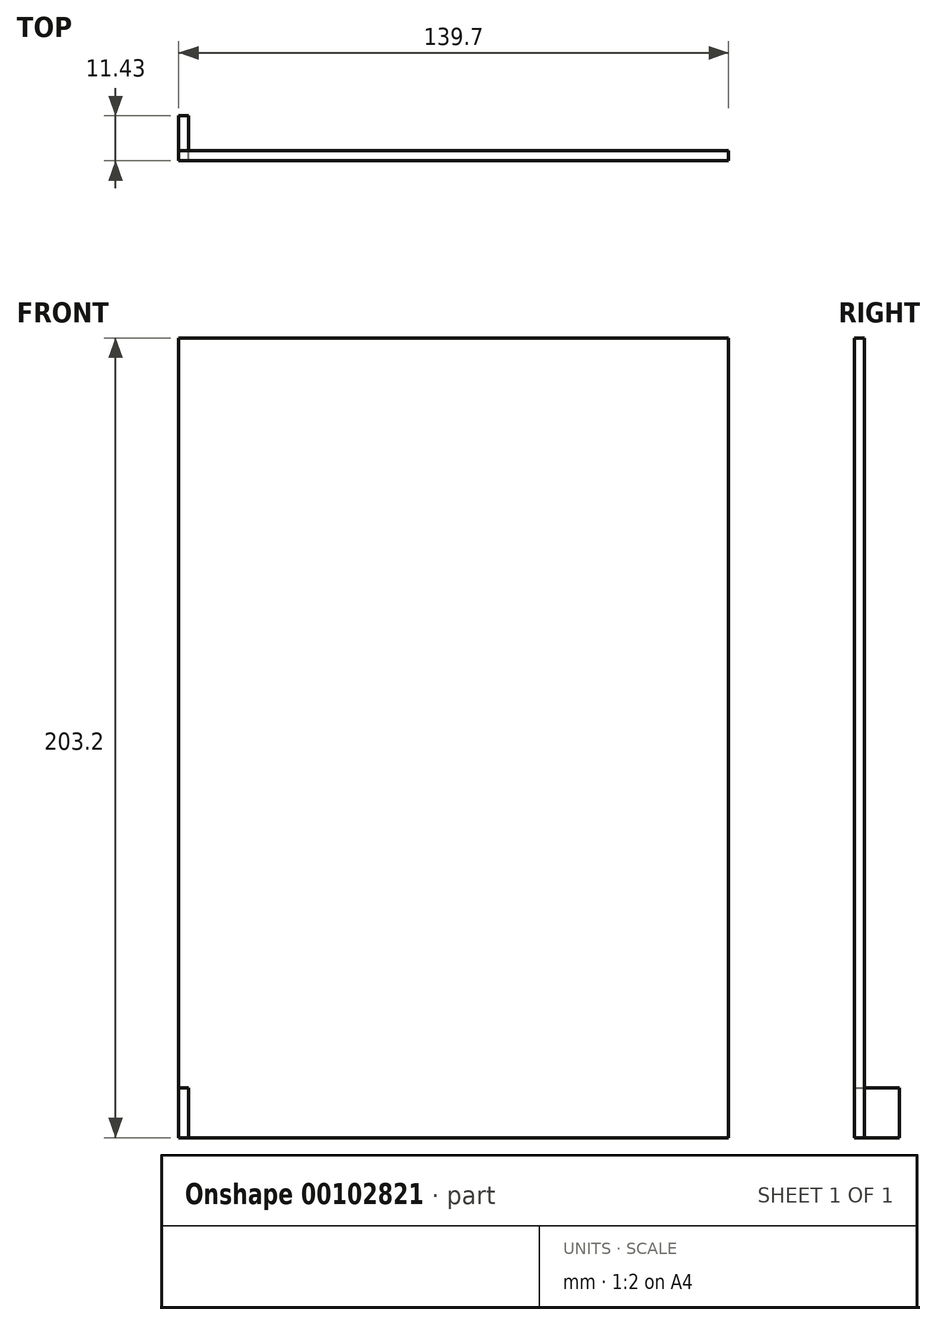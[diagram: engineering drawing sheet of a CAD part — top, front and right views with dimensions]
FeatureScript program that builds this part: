
annotation { "Feature Type Name" : "Feature", "Feature Type Description" : "" }
export const myFeature = defineFeature(function(context is Context, id is Id, definition is map)
    precondition{}
    {
        {
            var Q0;
            Q0=qCreatedBy(makeId("Front.planeOp"),FACE);
            var sketch = newSketch(context, id + "F0", { "sketchPlane" : qUnion([Q0])});
            skLineSegment(sketch, "E0.bottom", {"start": v(-105.57, -93.89) * mm, "end": v(34.13, -93.89) * mm});
            skLineSegment(sketch, "E0.top", {"start": v(-105.57, 109.31) * mm, "end": v(34.13, 109.31) * mm});
            skLineSegment(sketch, "E0.left", {"start": v(-105.57, -93.89) * mm, "end": v(-105.57, 109.31) * mm});
            skLineSegment(sketch, "E0.right", {"start": v(34.13, -93.89) * mm, "end": v(34.13, 109.31) * mm});
            skSolve(sketch);
        }
        {
            var Q0;
            Q0=makeQuery(id+"F0.imprint","IMPRINT",FACE,{"disambiguationData":[TD([[makeQuery(id+"F0.imprint","IMPRINT",EDGE,{"derivedFrom":sQuery(id+"F0.wireOp",EDGE,"E0.bottom")}),1.0]])]});
            extrude(context, id + "F1", {"entities" : qUnion([Q0]), "depth" : 2.54 * mm});
        }
        {
            var Q0;
            Q0=qCreatedBy(makeId("Front.planeOp"),FACE);
            cPlane(context, id + "F2", {"entities" : qUnion([Q0]), "cplaneType" : CPlaneType.OFFSET, "offset" : 6.35 * mm, "oppositeDirection" : true, "width" : 152.4 * mm, "height" : 152.4 * mm});
        }
        {
            var Q0;
            Q0=qCreatedBy(id+"F2.planeOp",FACE);
            var sketch = newSketch(context, id + "F3", { "sketchPlane" : qUnion([Q0])});
            skLineSegment(sketch, "E1.0.0", {"start": v(-105.57, -93.89) * mm, "end": v(-105.57, 109.31) * mm});
            skLineSegment(sketch, "E1.0.1", {"start": v(-105.57, 109.31) * mm, "end": v(34.13, 109.31) * mm});
            skLineSegment(sketch, "E1.0.2", {"start": v(34.13, 109.31) * mm, "end": v(34.13, -93.89) * mm});
            skLineSegment(sketch, "E1.0.3", {"start": v(34.13, -93.89) * mm, "end": v(-105.57, -93.89) * mm});
            skLineSegment(sketch, "E2.top", {"start": v(34.13, -81.19) * mm, "end": v(-105.57, -81.19) * mm});
            skLineSegment(sketch, "E2.left", {"start": v(34.13, -93.89) * mm, "end": v(34.13, -81.19) * mm});
            skLineSegment(sketch, "E2.right", {"start": v(-105.57, -93.89) * mm, "end": v(-105.57, -81.19) * mm});
            skSolve(sketch);
        }
        {
            var Q0;
            Q0=makeQuery(id+"F3.imprint","IMPRINT",FACE,{"disambiguationData":[TD([[makeQuery(id+"F3.imprint","IMPRINT",EDGE,{"derivedFrom":sQuery(id+"F3.wireOp",EDGE,"E1.0.3")}),-1.0]])]});
            var Q1;
            Q1=makeQuery(id+"F1.opExtrude","CAP_FACE",FACE,{"disambiguationData":[OSD([sQuery(id+"F0.wireOp",EDGE,"E0.bottom"),sQuery(id+"F0.wireOp",EDGE,"E0.top"),sQuery(id+"F0.wireOp",EDGE,"E0.left"),sQuery(id+"F0.wireOp",EDGE,"E0.right")])],"isStart":true});
            var Q2;
            Q2=makeQuery(id+"F1.opExtrude","CAP_FACE",FACE,{"disambiguationData":[OSD([sQuery(id+"F0.wireOp",EDGE,"E0.bottom"),sQuery(id+"F0.wireOp",EDGE,"E0.top"),sQuery(id+"F0.wireOp",EDGE,"E0.left"),sQuery(id+"F0.wireOp",EDGE,"E0.right")])],"isStart":true});
            extrude(context, id + "F4", {"entities" : qUnion([Q0, Q1, Q2]), "operationType" : NewBodyOperationType.ADD, "oppositeDirection" : true, "depth" : 2.54 * mm});
        }
        {
            var Q0;
            {var subQ0=sQuery(id+"F0.wireOp",EDGE,"E0.left");Q0=makeQuery(id+"F4.boolean.opBoolean","MERGE",FACE,{"derivedFrom":[makeQuery(id+"F1.opExtrude","SWEPT_FACE",FACE,{"disambiguationData":[OSD([subQ0])]}),makeQuery(id+"F4.opExtrude","SWEPT_FACE",FACE,{"disambiguationData":[OSD([subQ0])]})]});}
            var sketch = newSketch(context, id + "F5", { "sketchPlane" : qUnion([Q0])});
            skPoint(sketch, "E3.0", {"position": v(-8.9, -93.89) * mm});
            skPoint(sketch, "E4.0", {"position": v(2.54, -93.89) * mm});
            skPoint(sketch, "E5.0", {"position": v(-8.9, -81.19) * mm});
            skLineSegment(sketch, "E6.bottom", {"start": v(2.54, -93.89) * mm, "end": v(-8.9, -93.89) * mm});
            skLineSegment(sketch, "E6.top", {"start": v(2.54, -81.19) * mm, "end": v(-8.9, -81.19) * mm});
            skLineSegment(sketch, "E6.left", {"start": v(2.54, -93.89) * mm, "end": v(2.54, -81.19) * mm});
            skLineSegment(sketch, "E6.right", {"start": v(-8.9, -93.89) * mm, "end": v(-8.9, -81.19) * mm});
            skSolve(sketch);
        }
        {
            var Q0;
            {var subQ3=sQuery(id+"F5.wireOp",EDGE,"E6.right");Q0=makeQuery(id+"F5.imprint","IMPRINT",FACE,{"disambiguationData":[TD([[makeQuery(id+"F5.imprint","IMPRINT",EDGE,{"derivedFrom":subQ3}),-1.0]])]});}
            var Q1;
            {var subQ0=sQuery(id+"F5.wireOp",EDGE,"E6.left");Q1=makeQuery(id+"F5.imprint","IMPRINT",FACE,{"disambiguationData":[TD([[makeQuery(id+"F5.imprint","IMPRINT",EDGE,{"derivedFrom":subQ0}),1.0]])]});}
            extrude(context, id + "F6", {"entities" : qUnion([Q0, Q1]), "oppositeDirection" : true, "depth" : 2.54 * mm});
        }
    });
